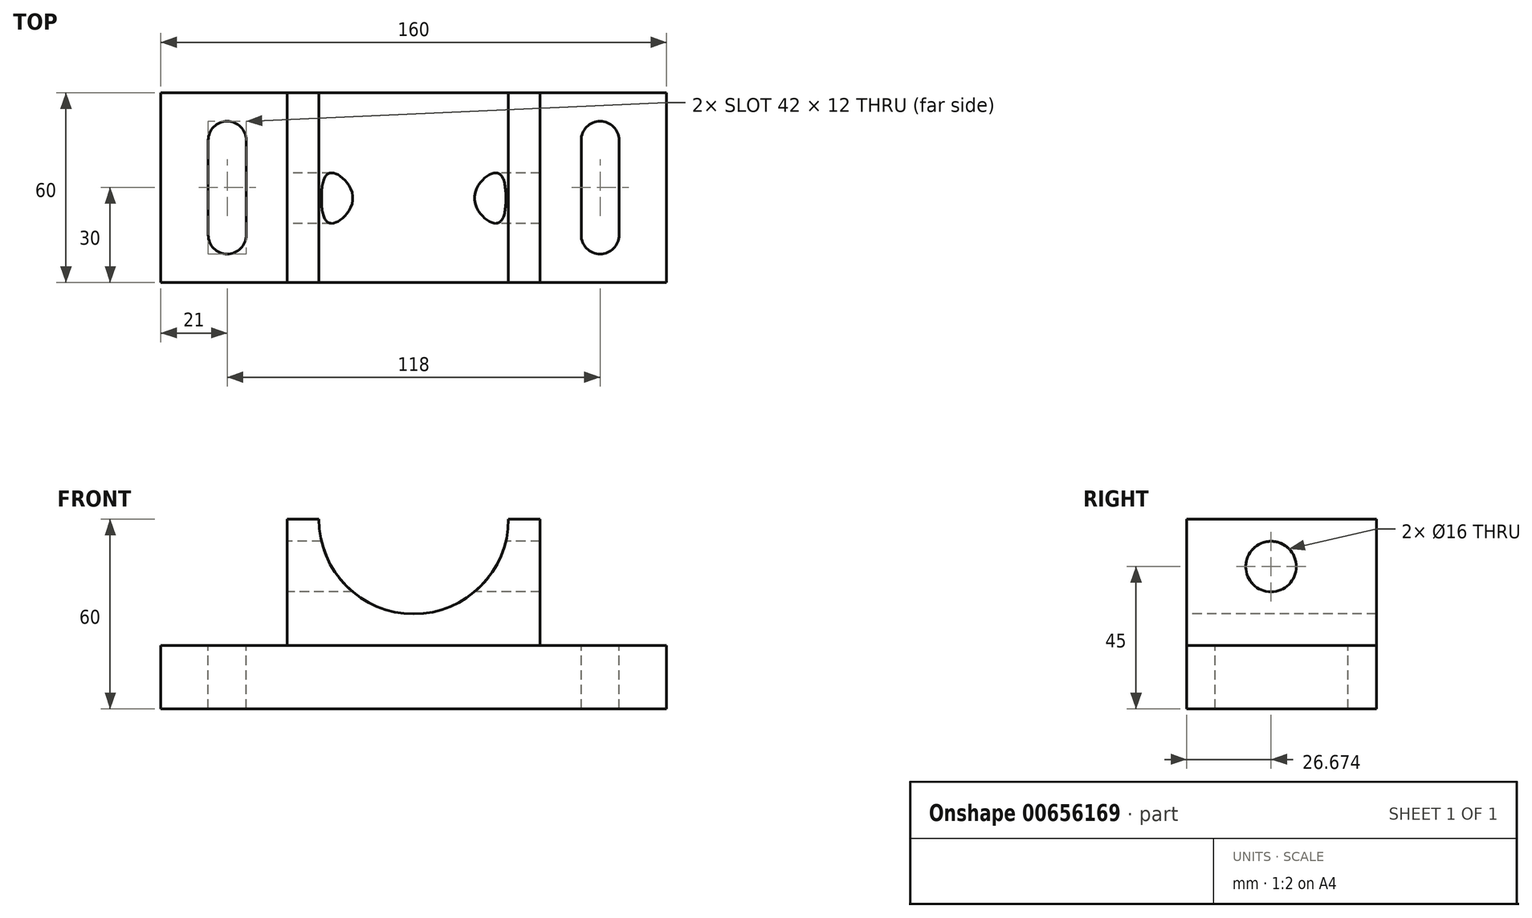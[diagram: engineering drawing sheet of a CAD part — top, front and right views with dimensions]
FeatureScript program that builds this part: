
annotation { "Feature Type Name" : "Feature", "Feature Type Description" : "" }
export const myFeature = defineFeature(function(context is Context, id is Id, definition is map)
    precondition{}
    {
        {
            var Q0;
            Q0=qCreatedBy(makeId("Front.planeOp"),FACE);
            var sketch = newSketch(context, id + "F0", { "sketchPlane" : qUnion([Q0])});
            skLineSegment(sketch, "E0.bottom", {"start": v(-66.06, 20) * mm, "end": v(93.94, 20) * mm});
            skLineSegment(sketch, "E0.top", {"start": v(-66.06, 0) * mm, "end": v(93.94, 0) * mm});
            skLineSegment(sketch, "E0.left", {"start": v(-66.06, 20) * mm, "end": v(-66.06, 0) * mm});
            skLineSegment(sketch, "E0.right", {"start": v(93.94, 20) * mm, "end": v(93.94, 0) * mm});
            skSolve(sketch);
        }
        {
            var Q0;
            Q0 = qSketchRegion(id + "F0", true);
            extrude(context, id + "F1", {"entities" : qUnion([Q0]), "depth" : 60 * mm, "offsetDistance" : 25 * mm});
        }
        {
            var Q0;
            Q0=makeQuery(id+"F1.opExtrude","CAP_FACE",FACE,{"disambiguationData":[OSD([sQuery(id+"F0.wireOp",EDGE,"E0.bottom"),sQuery(id+"F0.wireOp",EDGE,"E0.top"),sQuery(id+"F0.wireOp",EDGE,"E0.left"),sQuery(id+"F0.wireOp",EDGE,"E0.right")])],"isStart":false});
            var sketch = newSketch(context, id + "F2", { "sketchPlane" : qUnion([Q0])});
            skLineSegment(sketch, "E1", {"start": v(-66.06, 20) * mm, "end": v(-26.06, 20) * mm});
            skLineSegment(sketch, "E2", {"start": v(-26.06, 20) * mm, "end": v(-26.06, 60) * mm});
            skLineSegment(sketch, "E3", {"start": v(-26.06, 60) * mm, "end": v(-16.06, 60) * mm});
            skLineSegment(sketch, "E4", {"start": v(53.94, 60) * mm, "end": v(53.94, 20) * mm});
            skArc(sketch, "E5", {"start": v(-16.06, 60) * mm, "mid": v(13.94, 30) * mm, "end": v(43.94, 60) * mm});
            skLineSegment(sketch, "E6.trimOffspring", {"start": v(43.94, 60) * mm, "end": v(53.94, 60) * mm});
            skSolve(sketch);
        }
        {
            var Q0;
            Q0 = qSketchRegion(id + "F2", true);
            var Q1;
            {var subQ1=sQuery(id+"F2.wireOp",EDGE,"E2");Q1=makeQuery(id+"F2.imprint","IMPRINT",FACE,{"disambiguationData":[TD([[makeQuery(id+"F2.imprint","IMPRINT",EDGE,{"derivedFrom":subQ1}),-1.0]])]});}
            extrude(context, id + "F3", {"entities" : qUnion([Q0, Q1]), "oppositeDirection" : true, "depth" : 60 * mm, "offsetDistance" : 25 * mm});
        }
        {
            var Q0;
            Q0=makeQuery(id+"F3.opExtrude","SWEPT_FACE",FACE,{"disambiguationData":[OSD([sQuery(id+"F2.wireOp",EDGE,"E2")])]});
            var sketch = newSketch(context, id + "F4", { "sketchPlane" : qUnion([Q0])});
            skLineSegment(sketch, "E7", {"start": v(63.33, 0) * mm, "end": v(33.33, 0) * mm});
            skLineSegment(sketch, "E8", {"start": v(33.33, 45) * mm, "end": v(33.33, 0) * mm});
            skCircle(sketch, "E9", {"center": v(33.33, 45) * mm, "radius": 8 * mm});
            skSolve(sketch);
        }
        {
            var Q0;
            Q0 = qSketchRegion(id + "F4", true);
            extrude(context, id + "F5", {"entities" : qUnion([Q0]), "operationType" : NewBodyOperationType.REMOVE, "oppositeDirection" : true, "depth" : 80 * mm, "offsetDistance" : 25 * mm});
        }
        {
            var Q0;
            Q0=makeQuery(id+"F1.opExtrude","SWEPT_FACE",FACE,{"disambiguationData":[OSD([sQuery(id+"F0.wireOp",EDGE,"E0.bottom")])]});
            var sketch = newSketch(context, id + "F6", { "sketchPlane" : qUnion([Q0])});
            skLineSegment(sketch, "E10", {"start": v(93.94, 0) * mm, "end": v(93.94, -30) * mm});
            skLineSegment(sketch, "E11", {"start": v(93.94, -30) * mm, "end": v(78.94, -30) * mm});
            skLineSegment(sketch, "E12", {"start": v(78.94, -30) * mm, "end": v(78.94, -15) * mm});
            skLineSegment(sketch, "E13", {"start": v(78.94, -15) * mm, "end": v(78.94, -45) * mm});
            skLineSegment(sketch, "E14", {"start": v(66.94, -15) * mm, "end": v(66.94, -45) * mm});
            skArc(sketch, "E15", {"start": v(78.94, -15) * mm, "mid": v(72.94, -9) * mm, "end": v(66.94, -15) * mm});
            skArc(sketch, "E16", {"start": v(66.94, -45) * mm, "mid": v(72.94, -51) * mm, "end": v(78.94, -45) * mm});
            skLineSegment(sketch, "E17", {"start": v(-66.06, 0) * mm, "end": v(-66.06, -30) * mm});
            skLineSegment(sketch, "E18", {"start": v(-66.06, -30) * mm, "end": v(-51.06, -30) * mm});
            skLineSegment(sketch, "E19", {"start": v(-51.06, -30) * mm, "end": v(-51.06, -15) * mm});
            skLineSegment(sketch, "E20", {"start": v(-51.06, -15) * mm, "end": v(-51.06, -45) * mm});
            skLineSegment(sketch, "E21", {"start": v(-39.06, -45) * mm, "end": v(-45.06, -45) * mm});
            skLineSegment(sketch, "E22", {"start": v(-45.06, -45) * mm, "end": v(-39.06, -45) * mm});
            skLineSegment(sketch, "E23", {"start": v(-39.06, -15) * mm, "end": v(-39.06, -45) * mm});
            skArc(sketch, "E24", {"start": v(-39.06, -15) * mm, "mid": v(-45.06, -9) * mm, "end": v(-51.06, -15) * mm});
            skArc(sketch, "E25", {"start": v(-51.06, -45) * mm, "mid": v(-45.06, -51) * mm, "end": v(-39.06, -45) * mm});
            skSolve(sketch);
        }
        {
            var Q0;
            Q0 = qSketchRegion(id + "F6", true);
            extrude(context, id + "F7", {"entities" : qUnion([Q0]), "operationType" : NewBodyOperationType.REMOVE, "oppositeDirection" : true, "depth" : 20 * mm, "offsetDistance" : 25 * mm});
        }
    });
